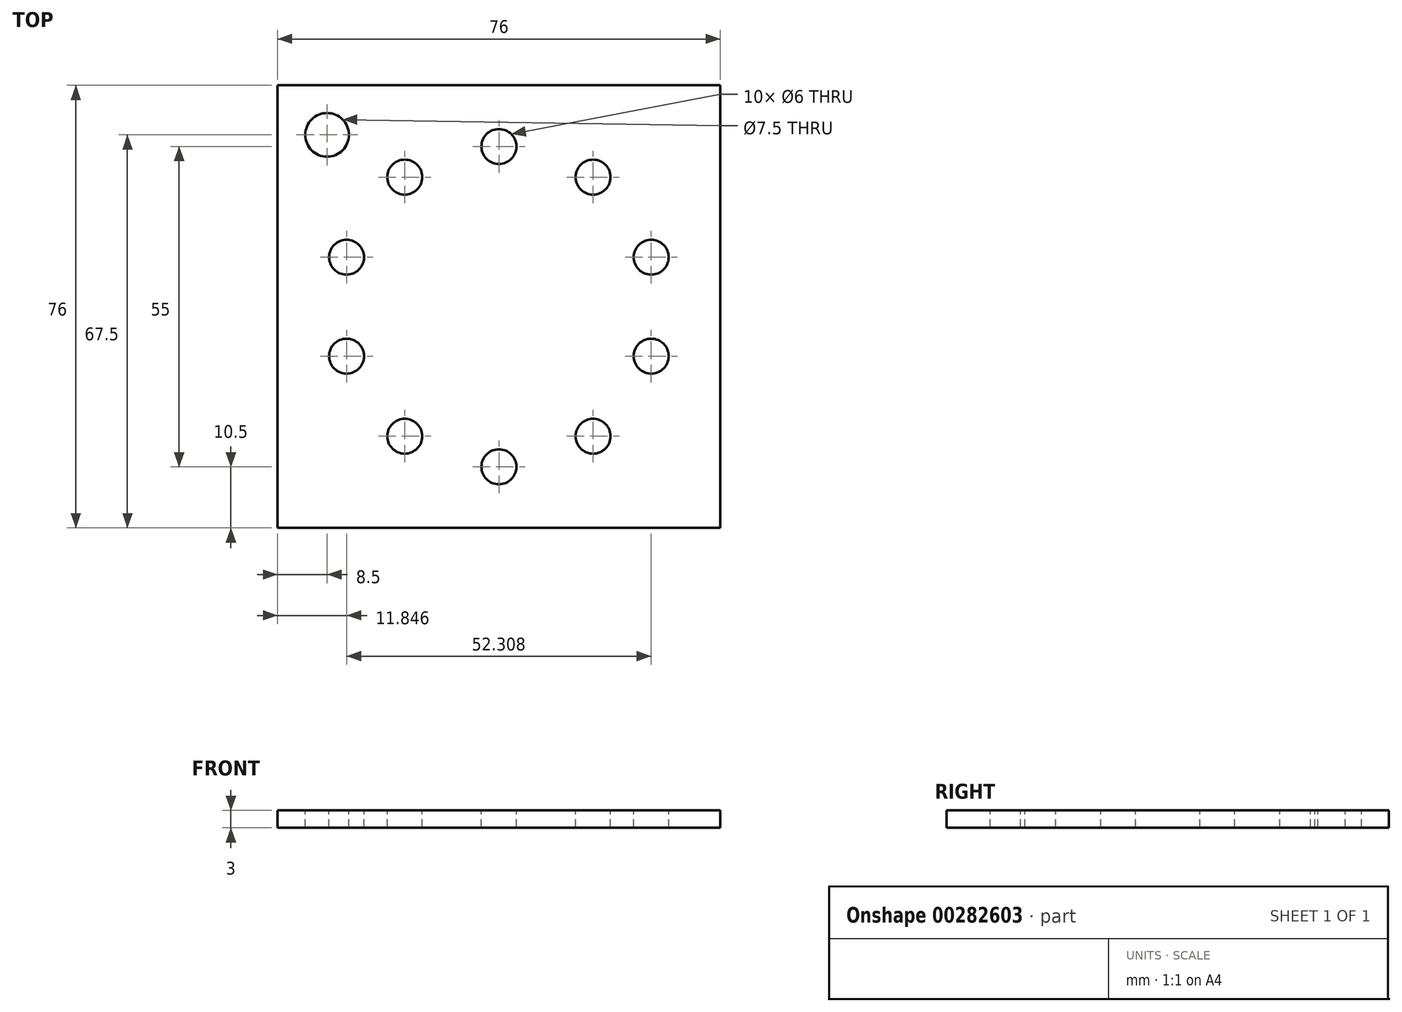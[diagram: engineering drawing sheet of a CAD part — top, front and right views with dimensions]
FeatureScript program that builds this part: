
annotation { "Feature Type Name" : "Feature", "Feature Type Description" : "" }
export const myFeature = defineFeature(function(context is Context, id is Id, definition is map)
    precondition{}
    {
        {
            var Q0;
            Q0=qCreatedBy(makeId("Top.planeOp"),FACE);
            var sketch = newSketch(context, id + "F0", { "sketchPlane" : qUnion([Q0])});
            skLineSegment(sketch, "E0.bottom", {"start": v(-38, 38) * mm, "end": v(38, 38) * mm});
            skLineSegment(sketch, "E0.top", {"start": v(-38, -38) * mm, "end": v(38, -38) * mm});
            skLineSegment(sketch, "E0.left", {"start": v(-38, 38) * mm, "end": v(-38, -38) * mm});
            skLineSegment(sketch, "E0.right", {"start": v(38, 38) * mm, "end": v(38, -38) * mm});
            skSolve(sketch);
        }
        {
            var Q0;
            Q0=makeQuery(id+"F0.imprint","IMPRINT",FACE,{"disambiguationData":[TD([[makeQuery(id+"F0.imprint","IMPRINT",EDGE,{"derivedFrom":sQuery(id+"F0.wireOp",EDGE,"E0.bottom")}),-1.0]])]});
            extrude(context, id + "F1", {"entities" : qUnion([Q0]), "depth" : 3 * mm});
        }
        {
            var Q0;
            Q0=makeQuery(id+"F1.opExtrude","CAP_FACE",FACE,{"disambiguationData":[OSD([sQuery(id+"F0.wireOp",EDGE,"E0.bottom"),sQuery(id+"F0.wireOp",EDGE,"E0.top"),sQuery(id+"F0.wireOp",EDGE,"E0.left"),sQuery(id+"F0.wireOp",EDGE,"E0.right")])],"isStart":false});
            var sketch = newSketch(context, id + "F2", { "sketchPlane" : qUnion([Q0])});
            skCircle(sketch, "E1", {"center": v(0, 0) * mm, "radius": 35 * mm});
            skCircle(sketch, "E2", {"center": v(0, 0) * mm, "radius": 27.5 * mm});
            skCircle(sketch, "E3", {"center": v(0, 27.5) * mm, "radius": 3 * mm});
            skCircle(sketch, "E4.1.0", {"center": v(-16.16, 22.25) * mm, "radius": 3 * mm});
            skCircle(sketch, "E4.2.0", {"center": v(-26.15, 8.5) * mm, "radius": 3 * mm});
            skCircle(sketch, "E4.3.0", {"center": v(-26.15, -8.5) * mm, "radius": 3 * mm});
            skCircle(sketch, "E4.4.0", {"center": v(-16.16, -22.25) * mm, "radius": 3 * mm});
            skCircle(sketch, "E4.5.0", {"center": v(0, -27.5) * mm, "radius": 3 * mm});
            skCircle(sketch, "E4.6.0", {"center": v(16.16, -22.25) * mm, "radius": 3 * mm});
            skCircle(sketch, "E4.7.0", {"center": v(26.15, -8.5) * mm, "radius": 3 * mm});
            skCircle(sketch, "E4.8.0", {"center": v(26.15, 8.5) * mm, "radius": 3 * mm});
            skCircle(sketch, "E4.9.0", {"center": v(16.16, 22.25) * mm, "radius": 3 * mm});
            skSolve(sketch);
        }
        {
            var Q0;
            {var subQ0=sQuery(id+"F2.wireOp",EDGE,"E4.4.0");var subQ1=sQuery(id+"F2.wireOp",EDGE,"E2");var subQ2=makeQuery(id+"F2.imprint","INTERSECT",VERTEX,{"disambiguationData":[OD(0.0)],"derivedFrom":[subQ1,subQ0]});Q0=makeQuery(id+"F2.imprint","IMPRINT",FACE,{"disambiguationData":[TD([[makeQuery(id+"F2.imprint","IMPRINT",EDGE,{"disambiguationData":[TD([[subQ2,-1.0]])],"derivedFrom":subQ1}),-1.0]])]});}
            var Q1;
            {var subQ0=sQuery(id+"F2.wireOp",EDGE,"E4.4.0");var subQ1=sQuery(id+"F2.wireOp",EDGE,"E2");var subQ2=makeQuery(id+"F2.imprint","INTERSECT",VERTEX,{"disambiguationData":[OD(0.0)],"derivedFrom":[subQ1,subQ0]});Q1=makeQuery(id+"F2.imprint","IMPRINT",FACE,{"disambiguationData":[TD([[makeQuery(id+"F2.imprint","IMPRINT",EDGE,{"disambiguationData":[TD([[subQ2,-1.0]])],"derivedFrom":subQ1}),1.0]])]});}
            var Q2;
            {var subQ0=sQuery(id+"F2.wireOp",EDGE,"E4.5.0");var subQ1=sQuery(id+"F2.wireOp",EDGE,"E2");var subQ2=makeQuery(id+"F2.imprint","INTERSECT",VERTEX,{"disambiguationData":[OD(0.0)],"derivedFrom":[subQ1,subQ0]});Q2=makeQuery(id+"F2.imprint","IMPRINT",FACE,{"disambiguationData":[TD([[makeQuery(id+"F2.imprint","IMPRINT",EDGE,{"disambiguationData":[TD([[subQ2,-1.0]])],"derivedFrom":subQ1}),-1.0]])]});}
            var Q3;
            {var subQ0=sQuery(id+"F2.wireOp",EDGE,"E4.5.0");var subQ1=sQuery(id+"F2.wireOp",EDGE,"E2");var subQ2=makeQuery(id+"F2.imprint","INTERSECT",VERTEX,{"disambiguationData":[OD(0.0)],"derivedFrom":[subQ1,subQ0]});Q3=makeQuery(id+"F2.imprint","IMPRINT",FACE,{"disambiguationData":[TD([[makeQuery(id+"F2.imprint","IMPRINT",EDGE,{"disambiguationData":[TD([[subQ2,-1.0]])],"derivedFrom":subQ1}),1.0]])]});}
            var Q4;
            {var subQ0=sQuery(id+"F2.wireOp",EDGE,"E4.6.0");var subQ1=sQuery(id+"F2.wireOp",EDGE,"E2");var subQ2=makeQuery(id+"F2.imprint","INTERSECT",VERTEX,{"disambiguationData":[OD(0.0)],"derivedFrom":[subQ1,subQ0]});Q4=makeQuery(id+"F2.imprint","IMPRINT",FACE,{"disambiguationData":[TD([[makeQuery(id+"F2.imprint","IMPRINT",EDGE,{"disambiguationData":[TD([[subQ2,-1.0]])],"derivedFrom":subQ1}),1.0]])]});}
            var Q5;
            {var subQ0=sQuery(id+"F2.wireOp",EDGE,"E4.6.0");var subQ1=sQuery(id+"F2.wireOp",EDGE,"E2");var subQ2=makeQuery(id+"F2.imprint","INTERSECT",VERTEX,{"disambiguationData":[OD(0.0)],"derivedFrom":[subQ1,subQ0]});Q5=makeQuery(id+"F2.imprint","IMPRINT",FACE,{"disambiguationData":[TD([[makeQuery(id+"F2.imprint","IMPRINT",EDGE,{"disambiguationData":[TD([[subQ2,-1.0]])],"derivedFrom":subQ1}),-1.0]])]});}
            var Q6;
            {var subQ0=sQuery(id+"F2.wireOp",EDGE,"E4.7.0");var subQ1=sQuery(id+"F2.wireOp",EDGE,"E2");var subQ2=makeQuery(id+"F2.imprint","INTERSECT",VERTEX,{"disambiguationData":[OD(0.0)],"derivedFrom":[subQ1,subQ0]});Q6=makeQuery(id+"F2.imprint","IMPRINT",FACE,{"disambiguationData":[TD([[makeQuery(id+"F2.imprint","IMPRINT",EDGE,{"disambiguationData":[TD([[subQ2,-1.0]])],"derivedFrom":subQ1}),-1.0]])]});}
            var Q7;
            {var subQ0=sQuery(id+"F2.wireOp",EDGE,"E4.7.0");var subQ1=sQuery(id+"F2.wireOp",EDGE,"E2");var subQ2=makeQuery(id+"F2.imprint","INTERSECT",VERTEX,{"disambiguationData":[OD(0.0)],"derivedFrom":[subQ1,subQ0]});Q7=makeQuery(id+"F2.imprint","IMPRINT",FACE,{"disambiguationData":[TD([[makeQuery(id+"F2.imprint","IMPRINT",EDGE,{"disambiguationData":[TD([[subQ2,-1.0]])],"derivedFrom":subQ1}),1.0]])]});}
            var Q8;
            {var subQ0=sQuery(id+"F2.wireOp",EDGE,"E4.8.0");var subQ1=sQuery(id+"F2.wireOp",EDGE,"E2");var subQ2=makeQuery(id+"F2.imprint","INTERSECT",VERTEX,{"disambiguationData":[OD(0.0)],"derivedFrom":[subQ1,subQ0]});Q8=makeQuery(id+"F2.imprint","IMPRINT",FACE,{"disambiguationData":[TD([[makeQuery(id+"F2.imprint","IMPRINT",EDGE,{"disambiguationData":[TD([[subQ2,1.0]])],"derivedFrom":subQ1}),1.0]])]});}
            var Q9;
            {var subQ0=sQuery(id+"F2.wireOp",EDGE,"E4.8.0");var subQ1=sQuery(id+"F2.wireOp",EDGE,"E2");var subQ2=makeQuery(id+"F2.imprint","INTERSECT",VERTEX,{"disambiguationData":[OD(0.0)],"derivedFrom":[subQ1,subQ0]});Q9=makeQuery(id+"F2.imprint","IMPRINT",FACE,{"disambiguationData":[TD([[makeQuery(id+"F2.imprint","IMPRINT",EDGE,{"disambiguationData":[TD([[subQ2,1.0]])],"derivedFrom":subQ1}),-1.0]])]});}
            var Q10;
            {var subQ0=sQuery(id+"F2.wireOp",EDGE,"E4.9.0");var subQ1=sQuery(id+"F2.wireOp",EDGE,"E2");var subQ2=makeQuery(id+"F2.imprint","INTERSECT",VERTEX,{"disambiguationData":[OD(0.0)],"derivedFrom":[subQ1,subQ0]});Q10=makeQuery(id+"F2.imprint","IMPRINT",FACE,{"disambiguationData":[TD([[makeQuery(id+"F2.imprint","IMPRINT",EDGE,{"disambiguationData":[TD([[subQ2,-1.0]])],"derivedFrom":subQ1}),-1.0]])]});}
            var Q11;
            {var subQ0=sQuery(id+"F2.wireOp",EDGE,"E4.9.0");var subQ1=sQuery(id+"F2.wireOp",EDGE,"E2");var subQ2=makeQuery(id+"F2.imprint","INTERSECT",VERTEX,{"disambiguationData":[OD(0.0)],"derivedFrom":[subQ1,subQ0]});Q11=makeQuery(id+"F2.imprint","IMPRINT",FACE,{"disambiguationData":[TD([[makeQuery(id+"F2.imprint","IMPRINT",EDGE,{"disambiguationData":[TD([[subQ2,-1.0]])],"derivedFrom":subQ1}),1.0]])]});}
            var Q12;
            {var subQ0=sQuery(id+"F2.wireOp",EDGE,"E3");var subQ1=sQuery(id+"F2.wireOp",EDGE,"E2");var subQ2=makeQuery(id+"F2.imprint","INTERSECT",VERTEX,{"disambiguationData":[OD(0.0)],"derivedFrom":[subQ1,subQ0]});Q12=makeQuery(id+"F2.imprint","IMPRINT",FACE,{"disambiguationData":[TD([[makeQuery(id+"F2.imprint","IMPRINT",EDGE,{"disambiguationData":[TD([[subQ2,-1.0]])],"derivedFrom":subQ1}),1.0]])]});}
            var Q13;
            {var subQ0=sQuery(id+"F2.wireOp",EDGE,"E3");var subQ1=sQuery(id+"F2.wireOp",EDGE,"E2");var subQ2=makeQuery(id+"F2.imprint","INTERSECT",VERTEX,{"disambiguationData":[OD(0.0)],"derivedFrom":[subQ1,subQ0]});Q13=makeQuery(id+"F2.imprint","IMPRINT",FACE,{"disambiguationData":[TD([[makeQuery(id+"F2.imprint","IMPRINT",EDGE,{"disambiguationData":[TD([[subQ2,-1.0]])],"derivedFrom":subQ1}),-1.0]])]});}
            var Q14;
            {var subQ0=sQuery(id+"F2.wireOp",EDGE,"E4.1.0");var subQ1=sQuery(id+"F2.wireOp",EDGE,"E2");var subQ2=makeQuery(id+"F2.imprint","INTERSECT",VERTEX,{"disambiguationData":[OD(0.0)],"derivedFrom":[subQ1,subQ0]});Q14=makeQuery(id+"F2.imprint","IMPRINT",FACE,{"disambiguationData":[TD([[makeQuery(id+"F2.imprint","IMPRINT",EDGE,{"disambiguationData":[TD([[subQ2,-1.0]])],"derivedFrom":subQ1}),-1.0]])]});}
            var Q15;
            {var subQ0=sQuery(id+"F2.wireOp",EDGE,"E4.1.0");var subQ1=sQuery(id+"F2.wireOp",EDGE,"E2");var subQ2=makeQuery(id+"F2.imprint","INTERSECT",VERTEX,{"disambiguationData":[OD(0.0)],"derivedFrom":[subQ1,subQ0]});Q15=makeQuery(id+"F2.imprint","IMPRINT",FACE,{"disambiguationData":[TD([[makeQuery(id+"F2.imprint","IMPRINT",EDGE,{"disambiguationData":[TD([[subQ2,-1.0]])],"derivedFrom":subQ1}),1.0]])]});}
            var Q16;
            {var subQ0=sQuery(id+"F2.wireOp",EDGE,"E4.2.0");var subQ1=sQuery(id+"F2.wireOp",EDGE,"E2");var subQ2=makeQuery(id+"F2.imprint","INTERSECT",VERTEX,{"disambiguationData":[OD(0.0)],"derivedFrom":[subQ1,subQ0]});Q16=makeQuery(id+"F2.imprint","IMPRINT",FACE,{"disambiguationData":[TD([[makeQuery(id+"F2.imprint","IMPRINT",EDGE,{"disambiguationData":[TD([[subQ2,-1.0]])],"derivedFrom":subQ1}),1.0]])]});}
            var Q17;
            {var subQ0=sQuery(id+"F2.wireOp",EDGE,"E4.2.0");var subQ1=sQuery(id+"F2.wireOp",EDGE,"E2");var subQ2=makeQuery(id+"F2.imprint","INTERSECT",VERTEX,{"disambiguationData":[OD(0.0)],"derivedFrom":[subQ1,subQ0]});Q17=makeQuery(id+"F2.imprint","IMPRINT",FACE,{"disambiguationData":[TD([[makeQuery(id+"F2.imprint","IMPRINT",EDGE,{"disambiguationData":[TD([[subQ2,-1.0]])],"derivedFrom":subQ1}),-1.0]])]});}
            var Q18;
            {var subQ0=sQuery(id+"F2.wireOp",EDGE,"E4.3.0");var subQ1=sQuery(id+"F2.wireOp",EDGE,"E2");var subQ2=makeQuery(id+"F2.imprint","INTERSECT",VERTEX,{"disambiguationData":[OD(0.0)],"derivedFrom":[subQ1,subQ0]});Q18=makeQuery(id+"F2.imprint","IMPRINT",FACE,{"disambiguationData":[TD([[makeQuery(id+"F2.imprint","IMPRINT",EDGE,{"disambiguationData":[TD([[subQ2,-1.0]])],"derivedFrom":subQ1}),1.0]])]});}
            var Q19;
            {var subQ0=sQuery(id+"F2.wireOp",EDGE,"E4.3.0");var subQ1=sQuery(id+"F2.wireOp",EDGE,"E2");var subQ2=makeQuery(id+"F2.imprint","INTERSECT",VERTEX,{"disambiguationData":[OD(0.0)],"derivedFrom":[subQ1,subQ0]});Q19=makeQuery(id+"F2.imprint","IMPRINT",FACE,{"disambiguationData":[TD([[makeQuery(id+"F2.imprint","IMPRINT",EDGE,{"disambiguationData":[TD([[subQ2,-1.0]])],"derivedFrom":subQ1}),-1.0]])]});}
            extrude(context, id + "F3", {"entities" : qUnion([Q0, Q1, Q2, Q3, Q4, Q5, Q6, Q7, Q8, Q9, Q10, Q11, Q12, Q13, Q14, Q15, Q16, Q17, Q18, Q19]), "operationType" : NewBodyOperationType.REMOVE, "oppositeDirection" : true, "depth" : 25 * mm});
        }
        {
            var Q0;
            Q0=makeQuery(id+"F1.opExtrude","CAP_FACE",FACE,{"disambiguationData":[OSD([sQuery(id+"F0.wireOp",EDGE,"E0.bottom"),sQuery(id+"F0.wireOp",EDGE,"E0.top"),sQuery(id+"F0.wireOp",EDGE,"E0.left"),sQuery(id+"F0.wireOp",EDGE,"E0.right")])],"isStart":false});
            var sketch = newSketch(context, id + "F4", { "sketchPlane" : qUnion([Q0])});
            skCircle(sketch, "E5", {"center": v(-29.5, 29.5) * mm, "radius": 3.75 * mm});
            skSolve(sketch);
        }
        {
            var Q0;
            Q0=makeQuery(id+"F4.imprint","IMPRINT",FACE,{"disambiguationData":[TD([[makeQuery(id+"F4.imprint","IMPRINT",EDGE,{"derivedFrom":sQuery(id+"F4.wireOp",EDGE,"E5")}),1.0]])]});
            extrude(context, id + "F5", {"entities" : qUnion([Q0]), "operationType" : NewBodyOperationType.REMOVE, "oppositeDirection" : true, "depth" : 25 * mm});
        }
    });
